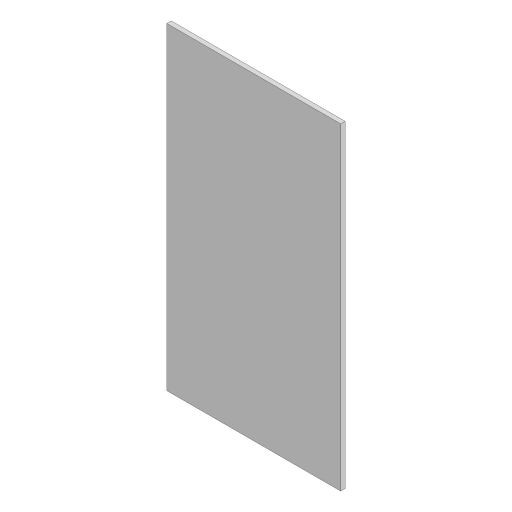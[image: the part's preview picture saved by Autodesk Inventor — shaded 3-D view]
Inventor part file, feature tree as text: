
AUTODESK INVENTOR PART (.ipt)
format: ipt  version: 2024 (Build 280153000, 153)  size: 81,408 bytes
history: native  units: in
note: dims shown in document units (in); Inventor stores cm internally (conversion verified against a paired STEP export)
features: extrude x1, sketch x1
ambient origin geometry x8: Origin, YZ Plane, XZ Plane, XY Plane, X Axis, Y Axis, Z Axis, Center Point
bodies: Solid1 (feature_tree)
feature tree (2):
  extrude  "Extrusion1"  Depth=93.8583in
  sketch  "Sketch1"  dims[d0=51.2992in d1=93.8583in d2=1.2992in d3=0.0in]
